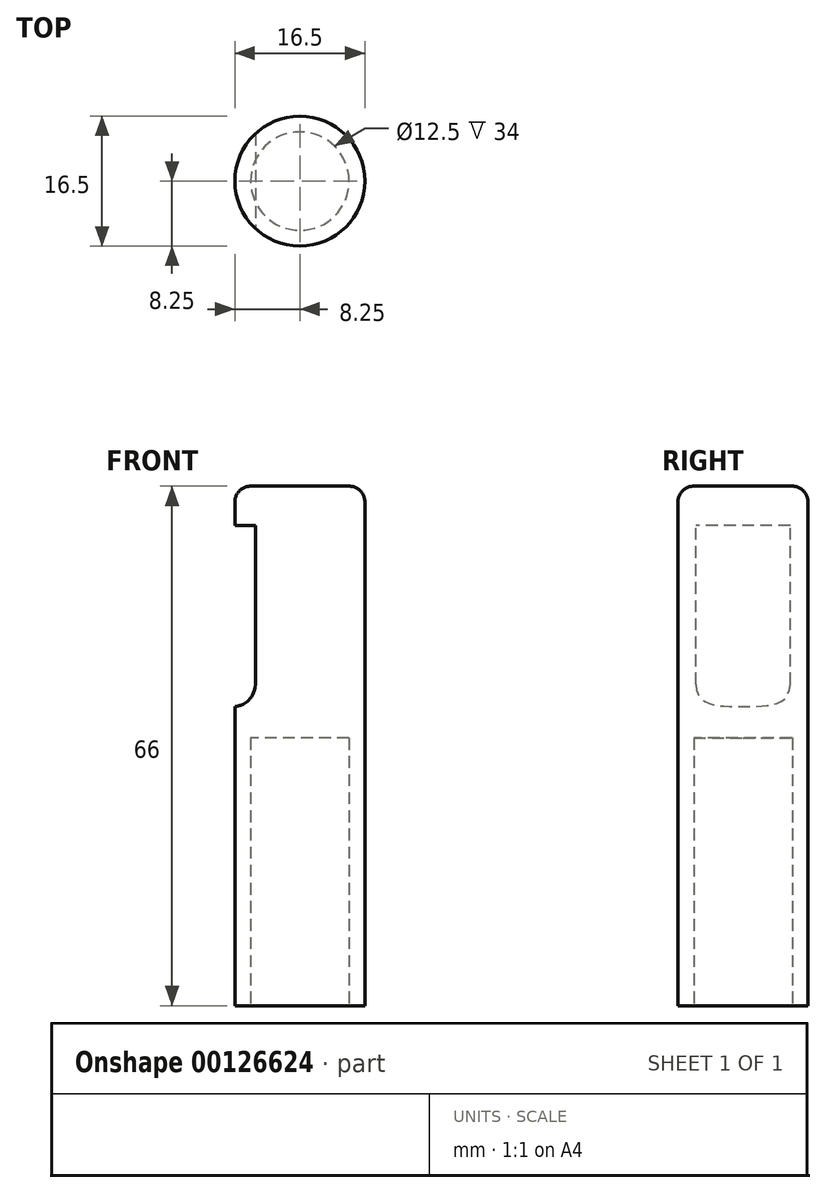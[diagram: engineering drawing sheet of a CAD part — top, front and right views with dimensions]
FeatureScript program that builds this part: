
annotation { "Feature Type Name" : "Feature", "Feature Type Description" : "" }
export const myFeature = defineFeature(function(context is Context, id is Id, definition is map)
    precondition{}
    {
        {
            var Q0;
            Q0=qCreatedBy(makeId("Top.planeOp"),FACE);
            var sketch = newSketch(context, id + "F0", { "sketchPlane" : qUnion([Q0])});
            skCircle(sketch, "E0", {"center": v(0, 0) * mm, "radius": 6.25 * mm});
            skCircle(sketch, "E1", {"center": v(0, 0) * mm, "radius": 8.25 * mm});
            skSolve(sketch);
        }
        {
            var Q0;
            Q0 = qSketchRegion(id + "F0", true);
            extrude(context, id + "F1", {"entities" : qUnion([Q0]), "depth" : 34 * mm, "offsetDistance" : 25 * mm});
        }
        {
            var Q0;
            Q0=makeQuery(id+"F1.opExtrude","CAP_FACE",FACE,{"disambiguationData":[OSD([sQuery(id+"F0.wireOp",EDGE,"E0"),sQuery(id+"F0.wireOp",EDGE,"E1")])],"isStart":false});
            var sketch = newSketch(context, id + "F2", { "sketchPlane" : qUnion([Q0])});
            skPoint(sketch, "E2.0", {"position": v(0, 0) * mm});
            skCircle(sketch, "E3", {"center": v(0, 0) * mm, "radius": 8.25 * mm});
            skSolve(sketch);
        }
        {
            var Q0;
            Q0 = qSketchRegion(id + "F2", true);
            extrude(context, id + "F3", {"entities" : qUnion([Q0]), "operationType" : NewBodyOperationType.ADD, "depth" : 32 * mm, "offsetDistance" : 25 * mm});
        }
        {
            var Q0;
            Q0=makeQuery(id+"F3.opExtrude","CAP_FACE",FACE,{"disambiguationData":[OSD([sQuery(id+"F2.wireOp",EDGE,"E3")])],"isStart":false});
            var sketch = newSketch(context, id + "F4", { "sketchPlane" : qUnion([Q0])});
            skCircle(sketch, "E4.0", {"center": v(0, 0) * mm, "radius": 8.25 * mm});
            skLineSegment(sketch, "E5", {"start": v(0, 0) * mm, "end": v(-8.25, 0) * mm, "construction": true});
            skLineSegment(sketch, "E6", {"start": v(-8.25, 0) * mm, "end": v(-8.25, 6) * mm, "construction": true});
            skLineSegment(sketch, "E7", {"start": v(-8.25, 0) * mm, "end": v(-8.25, -6) * mm, "construction": true});
            skLineSegment(sketch, "E8", {"start": v(-8.25, -6) * mm, "end": v(-5.66, -6) * mm, "construction": true});
            skLineSegment(sketch, "E9", {"start": v(-5.66, -6) * mm, "end": v(-5.66, 6) * mm, "construction": true});
            skLineSegment(sketch, "E10", {"start": v(-5.66, 6) * mm, "end": v(-8.25, 6) * mm, "construction": true});
            skLineSegment(sketch, "E11", {"start": v(-5.66, 6) * mm, "end": v(-5.66, -6) * mm});
            skArc(sketch, "E12", {"start": v(-5.66, 6) * mm, "mid": v(-8.25, 0) * mm, "end": v(-5.66, -6) * mm});
            skSolve(sketch);
        }
        {
            var Q0;
            {var subQ0=sQuery(id+"F4.wireOp",EDGE,"E11");Q0=makeQuery(id+"F4.imprint","IMPRINT",FACE,{"disambiguationData":[TD([[makeQuery(id+"F4.imprint","IMPRINT",EDGE,{"derivedFrom":subQ0}),-1.0]])]});}
            extrude(context, id + "F5", {"entities" : qUnion([Q0]), "operationType" : NewBodyOperationType.REMOVE, "oppositeDirection" : true, "depth" : 28 * mm, "offsetDistance" : 25 * mm});
        }
        {
            var Q0;
            {var subQ0=sQuery(id+"F4.wireOp",EDGE,"E11");Q0=makeQuery(id+"F4.imprint","IMPRINT",FACE,{"disambiguationData":[TD([[makeQuery(id+"F4.imprint","IMPRINT",EDGE,{"derivedFrom":subQ0}),-1.0]])]});}
            extrude(context, id + "F6", {"entities" : qUnion([Q0]), "operationType" : NewBodyOperationType.ADD, "oppositeDirection" : true, "depth" : 5 * mm, "offsetDistance" : 25 * mm});
        }
        {
            var Q0;
            Q0=makeQuery(id+"F6.opExtrude","CAP_EDGE",EDGE,{"disambiguationData":[OSD([sQuery(id+"F4.wireOp",EDGE,"E11")])],"isStart":false});
            var Q1;
            Q1=makeQuery(id+"F5.boolean.opBoolean","COPY",EDGE,{"derivedFrom":makeQuery(id+"F5.opExtrude","CAP_EDGE",EDGE,{"disambiguationData":[OSD([sQuery(id+"F4.wireOp",EDGE,"E11")])],"isStart":false})});
            fillet(context, id + "F7", {"entities" : qUnion([Q0, Q1]), "tangentPropagation" : true, "radius" : 2.8 * mm, "defaultsChanged" : true, "vertexSettings" : [], "allowEdgeOverflow" : false});
        }
        {
            var Q0;
            Q0=makeQuery(id+"F6.boolean.opBoolean","MERGE",EDGE,{"derivedFrom":[makeQuery(id+"F3.opExtrude","CAP_EDGE",EDGE,{"disambiguationData":[OSD([sQuery(id+"F2.wireOp",EDGE,"E3")])],"isStart":false}),makeQuery(id+"F6.opExtrude","CAP_EDGE",EDGE,{"disambiguationData":[OSD([sQuery(id+"F4.wireOp",EDGE,"E4.0")])],"isStart":true})]});
            fillet(context, id + "F8", {"entities" : qUnion([Q0]), "tangentPropagation" : true, "radius" : 2 * mm, "defaultsChanged" : true, "vertexSettings" : [], "allowEdgeOverflow" : false});
        }
    });
